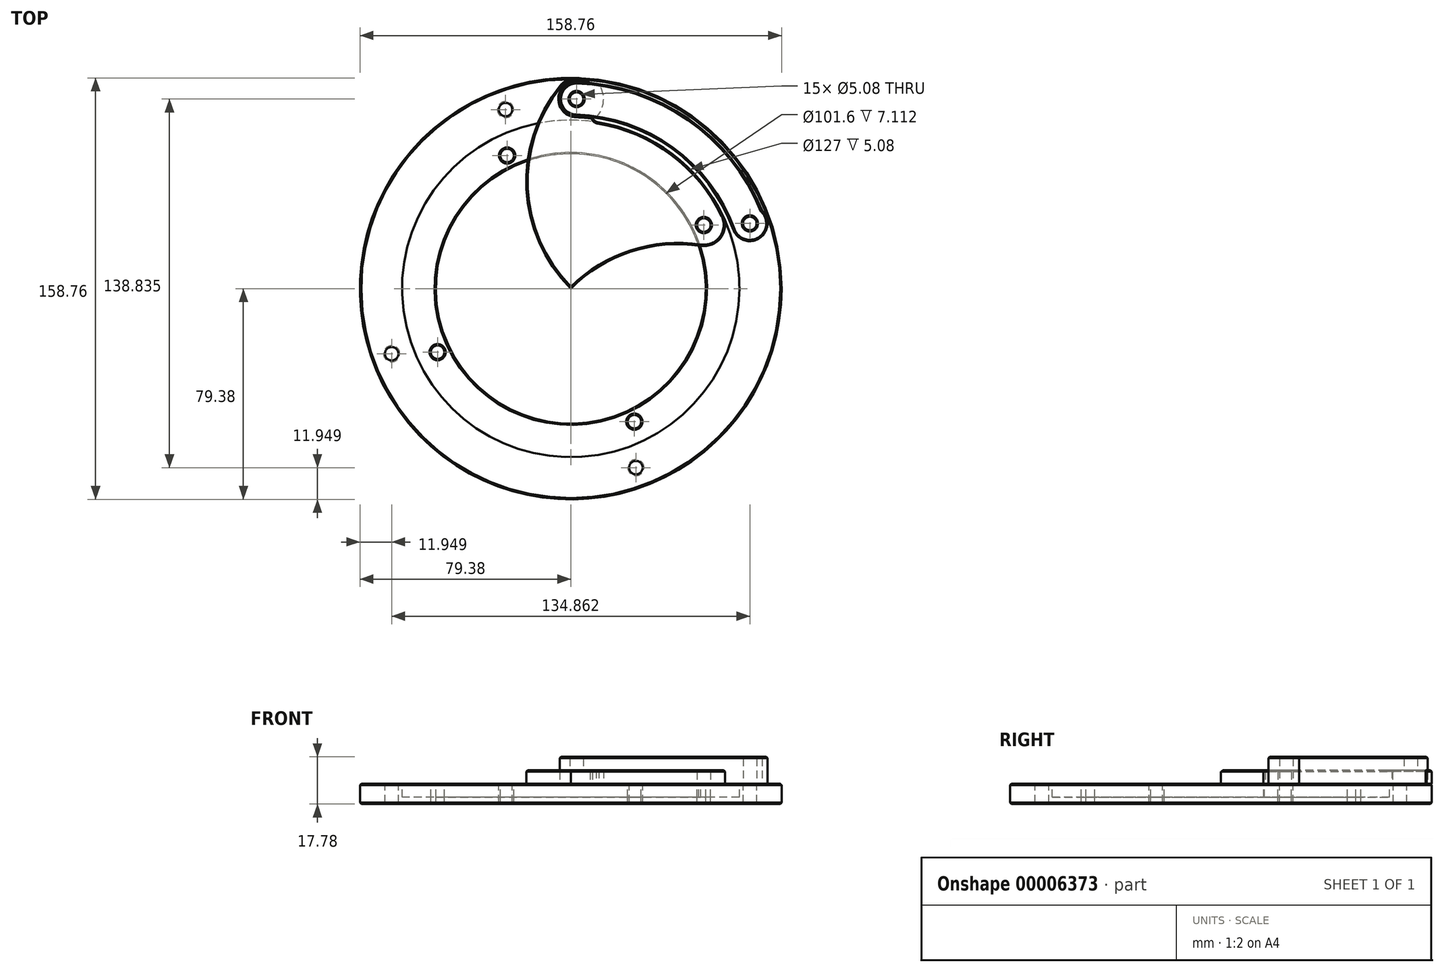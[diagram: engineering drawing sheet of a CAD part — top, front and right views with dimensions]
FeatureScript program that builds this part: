
annotation { "Feature Type Name" : "Feature", "Feature Type Description" : "" }
export const myFeature = defineFeature(function(context is Context, id is Id, definition is map)
    precondition{}
    {
        {
            var Q0;
            Q0=qCreatedBy(makeId("Top.planeOp"),FACE);
            var sketch = newSketch(context, id + "F0", { "sketchPlane" : qUnion([Q0])});
            skCircle(sketch, "E0", {"center": v(0, 0) * mm, "radius": 79.38 * mm});
            skCircle(sketch, "E1", {"center": v(0, 0) * mm, "radius": 63.5 * mm});
            skCircle(sketch, "E2", {"center": v(0, 0) * mm, "radius": 50.8 * mm});
            skLineSegment(sketch, "E3", {"start": v(0, 0) * mm, "end": v(-56.13, 56.13) * mm, "construction": true});
            skLineSegment(sketch, "E4", {"start": v(0, 0) * mm, "end": v(56.13, 56.13) * mm, "construction": true});
            skLineSegment(sketch, "E5", {"start": v(0, 0) * mm, "end": v(56.13, -56.13) * mm, "construction": true});
            skLineSegment(sketch, "E6", {"start": v(0, 0) * mm, "end": v(-56.13, -56.13) * mm, "construction": true});
            skCircle(sketch, "E7", {"center": v(40.41, 40.41) * mm, "radius": 57.15 * mm});
            skCircle(sketch, "E8", {"center": v(40.41, -40.41) * mm, "radius": 57.15 * mm});
            skCircle(sketch, "E9", {"center": v(2.18, 71.4) * mm, "radius": 7.94 * mm});
            skCircle(sketch, "E10", {"center": v(50.14, 23.95) * mm, "radius": 7.94 * mm});
            skCircle(sketch, "E11", {"center": v(2.18, 71.4) * mm, "radius": 2.54 * mm});
            skCircle(sketch, "E12", {"center": v(50.14, 23.95) * mm, "radius": 2.54 * mm});
            skCircle(sketch, "E13", {"center": v(10.61, 65.18) * mm, "radius": 2.54 * mm});
            skSolve(sketch);
        }
        {
            var Q0;
            {var subQ1=sQuery(id+"F0.wireOp",EDGE,"E7");var subQ3=sQuery(id+"F0.wireOp",EDGE,"E2");var subQ5=makeQuery(id+"F0.imprint","INTERSECT",VERTEX,{"disambiguationData":[OD(0.0)],"derivedFrom":[subQ3,subQ1]});Q0=makeQuery(id+"F0.imprint","IMPRINT",FACE,{"disambiguationData":[TD([[makeQuery(id+"F0.imprint","IMPRINT",EDGE,{"disambiguationData":[TD([[subQ5,1.0]])],"derivedFrom":subQ3}),1.0]])]});}
            var Q1;
            {var subQ3=sQuery(id+"F0.wireOp",EDGE,"E1");var subQ8=makeQuery(id+"F0.imprint","INTERSECT",VERTEX,{"derivedFrom":[subQ3,sQuery(id+"F0.wireOp",EDGE,"E9")]});Q1=makeQuery(id+"F0.imprint","IMPRINT",FACE,{"disambiguationData":[TD([[makeQuery(id+"F0.imprint","IMPRINT",EDGE,{"disambiguationData":[TD([[subQ8,1.0]])],"derivedFrom":subQ3}),1.0]])]});}
            var Q2;
            {var subQ0=sQuery(id+"F0.wireOp",EDGE,"E9");var subQ2=makeQuery(id+"F0.imprint","INTERSECT",VERTEX,{"derivedFrom":[sQuery(id+"F0.wireOp",EDGE,"E1"),subQ0]});Q2=makeQuery(id+"F0.imprint","IMPRINT",FACE,{"disambiguationData":[TD([[makeQuery(id+"F0.imprint","IMPRINT",EDGE,{"disambiguationData":[TD([[subQ2,1.0]])],"derivedFrom":subQ0}),1.0]])]});}
            var Q3;
            {var subQ0=sQuery(id+"F0.wireOp",EDGE,"E9");var subQ3=sQuery(id+"F0.wireOp",EDGE,"E1");var subQ4=makeQuery(id+"F0.imprint","INTERSECT",VERTEX,{"derivedFrom":[subQ3,subQ0]});Q3=makeQuery(id+"F0.imprint","IMPRINT",FACE,{"disambiguationData":[TD([[makeQuery(id+"F0.imprint","IMPRINT",EDGE,{"disambiguationData":[TD([[subQ4,-1.0]])],"derivedFrom":subQ3}),-1.0]])]});}
            var Q4;
            {var subQ0=sQuery(id+"F0.wireOp",EDGE,"E13");var subQ3=sQuery(id+"F0.wireOp",EDGE,"E1");var subQ4=makeQuery(id+"F0.imprint","INTERSECT",VERTEX,{"derivedFrom":[subQ3,subQ0]});Q4=makeQuery(id+"F0.imprint","IMPRINT",FACE,{"disambiguationData":[TD([[makeQuery(id+"F0.imprint","IMPRINT",EDGE,{"disambiguationData":[TD([[subQ4,-1.0]])],"derivedFrom":subQ3}),-1.0]])]});}
            var Q5;
            Q5=makeQuery(id+"F0.imprint","IMPRINT",FACE,{"disambiguationData":[TD([[makeQuery(id+"F0.imprint","IMPRINT",EDGE,{"derivedFrom":sQuery(id+"F0.wireOp",EDGE,"E12")}),-1.0]])]});
            var Q6;
            {var subQ0=sQuery(id+"F0.wireOp",EDGE,"E10");var subQ3=sQuery(id+"F0.wireOp",EDGE,"E2");var subQ4=makeQuery(id+"F0.imprint","INTERSECT",VERTEX,{"derivedFrom":[subQ3,subQ0]});Q6=makeQuery(id+"F0.imprint","IMPRINT",FACE,{"disambiguationData":[TD([[makeQuery(id+"F0.imprint","IMPRINT",EDGE,{"disambiguationData":[TD([[subQ4,1.0]])],"derivedFrom":subQ3}),-1.0]])]});}
            var Q7;
            {var subQ0=sQuery(id+"F0.wireOp",EDGE,"E10");var subQ1=sQuery(id+"F0.wireOp",EDGE,"E2");var subQ3=makeQuery(id+"F0.imprint","INTERSECT",VERTEX,{"disambiguationData":[OD(0.0)],"derivedFrom":[subQ1,subQ0]});Q7=makeQuery(id+"F0.imprint","IMPRINT",FACE,{"disambiguationData":[TD([[makeQuery(id+"F0.imprint","IMPRINT",EDGE,{"disambiguationData":[TD([[subQ3,-1.0]])],"derivedFrom":subQ1}),1.0]])]});}
            extrude(context, id + "F1", {"entities" : qUnion([Q0, Q1, Q2, Q3, Q4, Q5, Q6, Q7]), "depth" : 5.08 * mm});
        }
        {
            var Q0;
            {var subQ3=sQuery(id+"F0.wireOp",EDGE,"E0");var subQ5=sQuery(id+"F0.wireOp",EDGE,"E7");var subQ8=makeQuery(id+"F0.imprint","INTERSECT",VERTEX,{"disambiguationData":[OD(0.0)],"derivedFrom":[subQ3,subQ5]});Q0=makeQuery(id+"F0.imprint","IMPRINT",FACE,{"disambiguationData":[TD([[makeQuery(id+"F0.imprint","IMPRINT",EDGE,{"disambiguationData":[TD([[subQ8,-1.0]])],"derivedFrom":subQ3}),1.0]])]});}
            var Q1;
            {var subQ3=sQuery(id+"F0.wireOp",EDGE,"E1");var subQ5=sQuery(id+"F0.wireOp",EDGE,"E7");var subQ7=makeQuery(id+"F0.imprint","INTERSECT",VERTEX,{"disambiguationData":[OD(0.0)],"derivedFrom":[subQ3,subQ5]});Q1=makeQuery(id+"F0.imprint","IMPRINT",FACE,{"disambiguationData":[TD([[makeQuery(id+"F0.imprint","IMPRINT",EDGE,{"disambiguationData":[TD([[subQ7,-1.0]])],"derivedFrom":subQ3}),1.0]])]});}
            var Q2;
            {var subQ0=sQuery(id+"F0.wireOp",EDGE,"E8");var subQ3=sQuery(id+"F0.wireOp",EDGE,"E0");var subQ4=makeQuery(id+"F0.imprint","INTERSECT",VERTEX,{"disambiguationData":[OD(0.0)],"derivedFrom":[subQ3,subQ0]});Q2=makeQuery(id+"F0.imprint","IMPRINT",FACE,{"disambiguationData":[TD([[makeQuery(id+"F0.imprint","IMPRINT",EDGE,{"disambiguationData":[TD([[subQ4,-1.0]])],"derivedFrom":subQ3}),1.0]])]});}
            var Q3;
            {var subQ0=sQuery(id+"F0.wireOp",EDGE,"E8");var subQ3=sQuery(id+"F0.wireOp",EDGE,"E1");var subQ4=makeQuery(id+"F0.imprint","INTERSECT",VERTEX,{"disambiguationData":[OD(1.0)],"derivedFrom":[subQ3,subQ0]});Q3=makeQuery(id+"F0.imprint","IMPRINT",FACE,{"disambiguationData":[TD([[makeQuery(id+"F0.imprint","IMPRINT",EDGE,{"disambiguationData":[TD([[subQ4,-1.0]])],"derivedFrom":subQ3}),1.0]])]});}
            var Q4;
            {var subQ0=sQuery(id+"F0.wireOp",EDGE,"E8");var subQ4=sQuery(id+"F0.wireOp",EDGE,"E1");var subQ5=makeQuery(id+"F0.imprint","INTERSECT",VERTEX,{"disambiguationData":[OD(0.0)],"derivedFrom":[subQ4,subQ0]});Q4=makeQuery(id+"F0.imprint","IMPRINT",FACE,{"disambiguationData":[TD([[makeQuery(id+"F0.imprint","IMPRINT",EDGE,{"disambiguationData":[TD([[subQ5,1.0]])],"derivedFrom":subQ4}),1.0]])]});}
            var Q5;
            {var subQ5=sQuery(id+"F0.wireOp",EDGE,"E7");var subQ9=sQuery(id+"F0.wireOp",EDGE,"E0");var subQ11=makeQuery(id+"F0.imprint","INTERSECT",VERTEX,{"disambiguationData":[OD(0.0)],"derivedFrom":[subQ9,subQ5]});Q5=makeQuery(id+"F0.imprint","IMPRINT",FACE,{"disambiguationData":[TD([[makeQuery(id+"F0.imprint","IMPRINT",EDGE,{"disambiguationData":[TD([[subQ11,1.0]])],"derivedFrom":subQ9}),1.0]])]});}
            var Q6;
            {var subQ0=sQuery(id+"F0.wireOp",EDGE,"E8");var subQ3=sQuery(id+"F0.wireOp",EDGE,"E0");var subQ4=makeQuery(id+"F0.imprint","INTERSECT",VERTEX,{"disambiguationData":[OD(1.0)],"derivedFrom":[subQ3,subQ0]});Q6=makeQuery(id+"F0.imprint","IMPRINT",FACE,{"disambiguationData":[TD([[makeQuery(id+"F0.imprint","IMPRINT",EDGE,{"disambiguationData":[TD([[subQ4,1.0]])],"derivedFrom":subQ3}),1.0]])]});}
            var Q7;
            {var subQ0=sQuery(id+"F0.wireOp",EDGE,"E10");var subQ3=sQuery(id+"F0.wireOp",EDGE,"E1");var subQ4=makeQuery(id+"F0.imprint","INTERSECT",VERTEX,{"derivedFrom":[subQ3,subQ0]});Q7=makeQuery(id+"F0.imprint","IMPRINT",FACE,{"disambiguationData":[TD([[makeQuery(id+"F0.imprint","IMPRINT",EDGE,{"disambiguationData":[TD([[subQ4,1.0]])],"derivedFrom":subQ3}),1.0]])]});}
            var Q8;
            {var subQ0=sQuery(id+"F0.wireOp",EDGE,"E10");var subQ3=sQuery(id+"F0.wireOp",EDGE,"E1");var subQ4=makeQuery(id+"F0.imprint","INTERSECT",VERTEX,{"derivedFrom":[subQ3,subQ0]});Q8=makeQuery(id+"F0.imprint","IMPRINT",FACE,{"disambiguationData":[TD([[makeQuery(id+"F0.imprint","IMPRINT",EDGE,{"disambiguationData":[TD([[subQ4,-1.0]])],"derivedFrom":subQ3}),1.0]])]});}
            var Q9;
            Q9=makeQuery(id+"F0.imprint","IMPRINT",FACE,{"disambiguationData":[TD([[makeQuery(id+"F0.imprint","IMPRINT",EDGE,{"derivedFrom":sQuery(id+"F0.wireOp",EDGE,"E12")}),-1.0]])]});
            var Q10;
            {var subQ0=sQuery(id+"F0.wireOp",EDGE,"E10");var subQ3=sQuery(id+"F0.wireOp",EDGE,"E2");var subQ4=makeQuery(id+"F0.imprint","INTERSECT",VERTEX,{"derivedFrom":[subQ3,subQ0]});Q10=makeQuery(id+"F0.imprint","IMPRINT",FACE,{"disambiguationData":[TD([[makeQuery(id+"F0.imprint","IMPRINT",EDGE,{"disambiguationData":[TD([[subQ4,1.0]])],"derivedFrom":subQ3}),-1.0]])]});}
            var Q11;
            {var subQ0=sQuery(id+"F0.wireOp",EDGE,"E13");var subQ2=makeQuery(id+"F0.imprint","INTERSECT",VERTEX,{"derivedFrom":[sQuery(id+"F0.wireOp",EDGE,"E1"),subQ0]});Q11=makeQuery(id+"F0.imprint","IMPRINT",FACE,{"disambiguationData":[TD([[makeQuery(id+"F0.imprint","IMPRINT",EDGE,{"disambiguationData":[TD([[subQ2,1.0]])],"derivedFrom":subQ0}),1.0]])]});}
            var Q12;
            Q12=makeQuery(id+"F0.imprint","IMPRINT",FACE,{"disambiguationData":[TD([[makeQuery(id+"F0.imprint","IMPRINT",EDGE,{"derivedFrom":sQuery(id+"F0.wireOp",EDGE,"E11")}),-1.0]])]});
            var Q13;
            {var subQ0=sQuery(id+"F0.wireOp",EDGE,"E9");var subQ3=sQuery(id+"F0.wireOp",EDGE,"E1");var subQ4=makeQuery(id+"F0.imprint","INTERSECT",VERTEX,{"derivedFrom":[subQ3,subQ0]});Q13=makeQuery(id+"F0.imprint","IMPRINT",FACE,{"disambiguationData":[TD([[makeQuery(id+"F0.imprint","IMPRINT",EDGE,{"disambiguationData":[TD([[subQ4,-1.0]])],"derivedFrom":subQ3}),-1.0]])]});}
            var Q14;
            {var subQ0=sQuery(id+"F0.wireOp",EDGE,"E13");var subQ3=sQuery(id+"F0.wireOp",EDGE,"E1");var subQ4=makeQuery(id+"F0.imprint","INTERSECT",VERTEX,{"derivedFrom":[subQ3,subQ0]});Q14=makeQuery(id+"F0.imprint","IMPRINT",FACE,{"disambiguationData":[TD([[makeQuery(id+"F0.imprint","IMPRINT",EDGE,{"disambiguationData":[TD([[subQ4,-1.0]])],"derivedFrom":subQ3}),-1.0]])]});}
            var Q15;
            Q15=makeQuery(id+"F0.imprint","IMPRINT",FACE,{"disambiguationData":[TD([[makeQuery(id+"F0.imprint","IMPRINT",EDGE,{"derivedFrom":sQuery(id+"F0.wireOp",EDGE,"E11")}),1.0]])]});
            var Q16;
            {var subQ3=sQuery(id+"F0.wireOp",EDGE,"E0");var subQ6=sQuery(id+"F0.wireOp",EDGE,"E9");var subQ10=makeQuery(id+"F0.imprint","INTERSECT",VERTEX,{"derivedFrom":[subQ3,subQ6]});Q16=makeQuery(id+"F0.imprint","IMPRINT",FACE,{"disambiguationData":[TD([[makeQuery(id+"F0.imprint","IMPRINT",EDGE,{"disambiguationData":[TD([[subQ10,1.0]])],"derivedFrom":subQ3}),1.0]])]});}
            extrude(context, id + "F2", {"entities" : qUnion([Q0, Q1, Q2, Q3, Q4, Q5, Q6, Q7, Q8, Q9, Q10, Q11, Q12, Q13, Q14, Q15, Q16]), "oppositeDirection" : true, "depth" : 7.62 * mm});
        }
        {
            var Q0;
            Q0=qCreatedBy(makeId("Top.planeOp"),FACE);
            var sketch = newSketch(context, id + "F3", { "sketchPlane" : qUnion([Q0])});
            skLineSegment(sketch, "E14", {"start": v(0, 0) * mm, "end": v(126.68, 0) * mm, "construction": true});
            skLineSegment(sketch, "E15", {"start": v(0, 0) * mm, "end": v(115.08, 41.89) * mm, "construction": true});
            skCircle(sketch, "E16", {"center": v(0, 0) * mm, "radius": 71.76 * mm});
            skCircle(sketch, "E17", {"center": v(67.43, 24.54) * mm, "radius": 2.54 * mm});
            skCircle(sketch, "E18", {"center": v(2.18, 71.4) * mm, "radius": 2.54 * mm});
            skCircle(sketch, "E19", {"center": v(2.18, 71.4) * mm, "radius": 6.35 * mm});
            skCircle(sketch, "E20", {"center": v(0, 0) * mm, "radius": 65.09 * mm});
            skCircle(sketch, "E21", {"center": v(0, 0) * mm, "radius": 77.79 * mm});
            skCircle(sketch, "E22", {"center": v(2.18, 71.4) * mm, "radius": 10.16 * mm});
            skCircle(sketch, "E23", {"center": v(67.43, 24.54) * mm, "radius": 6.67 * mm});
            skSolve(sketch);
        }
        {
            var Q0;
            {var subQ0=sQuery(id+"F3.wireOp",EDGE,"E23");var subQ3=sQuery(id+"F3.wireOp",EDGE,"E16");var subQ4=makeQuery(id+"F3.imprint","INTERSECT",VERTEX,{"disambiguationData":[OD(1.0)],"derivedFrom":[subQ3,subQ0]});Q0=makeQuery(id+"F3.imprint","IMPRINT",FACE,{"disambiguationData":[TD([[makeQuery(id+"F3.imprint","IMPRINT",EDGE,{"disambiguationData":[TD([[subQ4,-1.0]])],"derivedFrom":subQ3}),1.0]])]});}
            var Q1;
            {var subQ2=sQuery(id+"F3.wireOp",EDGE,"E16");var subQ5=sQuery(id+"F3.wireOp",EDGE,"E17");var subQ7=makeQuery(id+"F3.imprint","INTERSECT",VERTEX,{"disambiguationData":[OD(0.0)],"derivedFrom":[subQ2,subQ5]});Q1=makeQuery(id+"F3.imprint","IMPRINT",FACE,{"disambiguationData":[TD([[makeQuery(id+"F3.imprint","IMPRINT",EDGE,{"disambiguationData":[TD([[subQ7,1.0]])],"derivedFrom":subQ2}),1.0]])]});}
            var Q2;
            {var subQ1=sQuery(id+"F3.wireOp",EDGE,"E16");var subQ7=sQuery(id+"F3.wireOp",EDGE,"E17");var subQ9=makeQuery(id+"F3.imprint","INTERSECT",VERTEX,{"disambiguationData":[OD(0.0)],"derivedFrom":[subQ1,subQ7]});Q2=makeQuery(id+"F3.imprint","IMPRINT",FACE,{"disambiguationData":[TD([[makeQuery(id+"F3.imprint","IMPRINT",EDGE,{"disambiguationData":[TD([[subQ9,1.0]])],"derivedFrom":subQ1}),-1.0]])]});}
            var Q3;
            {var subQ0=sQuery(id+"F3.wireOp",EDGE,"E23");var subQ1=sQuery(id+"F3.wireOp",EDGE,"E16");var subQ2=makeQuery(id+"F3.imprint","INTERSECT",VERTEX,{"disambiguationData":[OD(1.0)],"derivedFrom":[subQ1,subQ0]});Q3=makeQuery(id+"F3.imprint","IMPRINT",FACE,{"disambiguationData":[TD([[makeQuery(id+"F3.imprint","IMPRINT",EDGE,{"disambiguationData":[TD([[subQ2,-1.0]])],"derivedFrom":subQ1}),-1.0]])]});}
            var Q4;
            {var subQ0=sQuery(id+"F3.wireOp",EDGE,"E23");var subQ1=sQuery(id+"F3.wireOp",EDGE,"E21");var subQ3=makeQuery(id+"F3.imprint","INTERSECT",VERTEX,{"disambiguationData":[OD(0.0)],"derivedFrom":[subQ1,subQ0]});Q4=makeQuery(id+"F3.imprint","IMPRINT",FACE,{"disambiguationData":[TD([[makeQuery(id+"F3.imprint","IMPRINT",EDGE,{"disambiguationData":[TD([[subQ3,1.0]])],"derivedFrom":subQ1}),-1.0]])]});}
            var Q5;
            {var subQ0=sQuery(id+"F3.wireOp",EDGE,"E22");var subQ1=sQuery(id+"F3.wireOp",EDGE,"E16");var subQ2=makeQuery(id+"F3.imprint","INTERSECT",VERTEX,{"disambiguationData":[OD(0.0)],"derivedFrom":[subQ1,subQ0]});Q5=makeQuery(id+"F3.imprint","IMPRINT",FACE,{"disambiguationData":[TD([[makeQuery(id+"F3.imprint","IMPRINT",EDGE,{"disambiguationData":[TD([[subQ2,-1.0]])],"derivedFrom":subQ1}),-1.0]])]});}
            var Q6;
            {var subQ0=sQuery(id+"F3.wireOp",EDGE,"E19");var subQ2=sQuery(id+"F3.wireOp",EDGE,"E16");var subQ3=makeQuery(id+"F3.imprint","INTERSECT",VERTEX,{"disambiguationData":[OD(0.0)],"derivedFrom":[subQ2,subQ0]});Q6=makeQuery(id+"F3.imprint","IMPRINT",FACE,{"disambiguationData":[TD([[makeQuery(id+"F3.imprint","IMPRINT",EDGE,{"disambiguationData":[TD([[subQ3,-1.0]])],"derivedFrom":subQ2}),-1.0]])]});}
            var Q7;
            {var subQ0=sQuery(id+"F3.wireOp",EDGE,"E19");var subQ2=sQuery(id+"F3.wireOp",EDGE,"E16");var subQ3=makeQuery(id+"F3.imprint","INTERSECT",VERTEX,{"disambiguationData":[OD(0.0)],"derivedFrom":[subQ2,subQ0]});Q7=makeQuery(id+"F3.imprint","IMPRINT",FACE,{"disambiguationData":[TD([[makeQuery(id+"F3.imprint","IMPRINT",EDGE,{"disambiguationData":[TD([[subQ3,-1.0]])],"derivedFrom":subQ2}),1.0]])]});}
            var Q8;
            {var subQ0=sQuery(id+"F3.wireOp",EDGE,"E22");var subQ3=sQuery(id+"F3.wireOp",EDGE,"E16");var subQ4=makeQuery(id+"F3.imprint","INTERSECT",VERTEX,{"disambiguationData":[OD(0.0)],"derivedFrom":[subQ3,subQ0]});Q8=makeQuery(id+"F3.imprint","IMPRINT",FACE,{"disambiguationData":[TD([[makeQuery(id+"F3.imprint","IMPRINT",EDGE,{"disambiguationData":[TD([[subQ4,-1.0]])],"derivedFrom":subQ3}),1.0]])]});}
            extrude(context, id + "F4", {"entities" : qUnion([Q0, Q1, Q2, Q3, Q4, Q5, Q6, Q7, Q8]), "depth" : 10.16 * mm});
        }
        {
            var Q0;
            {var subQ0=sQuery(id+"F3.wireOp",EDGE,"E19");var subQ2=sQuery(id+"F3.wireOp",EDGE,"E16");var subQ3=makeQuery(id+"F3.imprint","INTERSECT",VERTEX,{"disambiguationData":[OD(0.0)],"derivedFrom":[subQ2,subQ0]});Q0=makeQuery(id+"F3.imprint","IMPRINT",FACE,{"disambiguationData":[TD([[makeQuery(id+"F3.imprint","IMPRINT",EDGE,{"disambiguationData":[TD([[subQ3,-1.0]])],"derivedFrom":subQ2}),1.0]])]});}
            var Q1;
            {var subQ0=sQuery(id+"F3.wireOp",EDGE,"E19");var subQ2=sQuery(id+"F3.wireOp",EDGE,"E16");var subQ3=makeQuery(id+"F3.imprint","INTERSECT",VERTEX,{"disambiguationData":[OD(0.0)],"derivedFrom":[subQ2,subQ0]});Q1=makeQuery(id+"F3.imprint","IMPRINT",FACE,{"disambiguationData":[TD([[makeQuery(id+"F3.imprint","IMPRINT",EDGE,{"disambiguationData":[TD([[subQ3,-1.0]])],"derivedFrom":subQ2}),-1.0]])]});}
            var Q2;
            {var subQ0=sQuery(id+"F3.wireOp",EDGE,"E22");var subQ1=sQuery(id+"F3.wireOp",EDGE,"E16");var subQ2=makeQuery(id+"F3.imprint","INTERSECT",VERTEX,{"disambiguationData":[OD(0.0)],"derivedFrom":[subQ1,subQ0]});Q2=makeQuery(id+"F3.imprint","IMPRINT",FACE,{"disambiguationData":[TD([[makeQuery(id+"F3.imprint","IMPRINT",EDGE,{"disambiguationData":[TD([[subQ2,-1.0]])],"derivedFrom":subQ1}),-1.0]])]});}
            var Q3;
            {var subQ0=sQuery(id+"F3.wireOp",EDGE,"E22");var subQ3=sQuery(id+"F3.wireOp",EDGE,"E16");var subQ4=makeQuery(id+"F3.imprint","INTERSECT",VERTEX,{"disambiguationData":[OD(0.0)],"derivedFrom":[subQ3,subQ0]});Q3=makeQuery(id+"F3.imprint","IMPRINT",FACE,{"disambiguationData":[TD([[makeQuery(id+"F3.imprint","IMPRINT",EDGE,{"disambiguationData":[TD([[subQ4,-1.0]])],"derivedFrom":subQ3}),1.0]])]});}
            extrude(context, id + "F5", {"entities" : qUnion([Q0, Q1, Q2, Q3]), "operationType" : NewBodyOperationType.REMOVE, "depth" : 5.08 * mm});
        }
        {
            var Q0;
            {var subQ0=sQuery(id+"F3.wireOp",EDGE,"E17");var subQ1=sQuery(id+"F3.wireOp",EDGE,"E16");var subQ3=makeQuery(id+"F3.imprint","INTERSECT",VERTEX,{"disambiguationData":[OD(0.0)],"derivedFrom":[subQ1,subQ0]});Q0=makeQuery(id+"F3.imprint","IMPRINT",FACE,{"disambiguationData":[TD([[makeQuery(id+"F3.imprint","IMPRINT",EDGE,{"disambiguationData":[TD([[subQ3,-1.0]])],"derivedFrom":subQ1}),-1.0]])]});}
            var Q1;
            {var subQ0=sQuery(id+"F3.wireOp",EDGE,"E17");var subQ1=sQuery(id+"F3.wireOp",EDGE,"E16");var subQ3=makeQuery(id+"F3.imprint","INTERSECT",VERTEX,{"disambiguationData":[OD(0.0)],"derivedFrom":[subQ1,subQ0]});Q1=makeQuery(id+"F3.imprint","IMPRINT",FACE,{"disambiguationData":[TD([[makeQuery(id+"F3.imprint","IMPRINT",EDGE,{"disambiguationData":[TD([[subQ3,-1.0]])],"derivedFrom":subQ1}),1.0]])]});}
            extrude(context, id + "F6", {"entities" : qUnion([Q0, Q1]), "operationType" : NewBodyOperationType.REMOVE, "oppositeDirection" : true, "depth" : 25.4 * mm});
        }
        {
            var Q0;
            Q0=qCreatedBy(makeId("Front.planeOp"),FACE);
            var sketch = newSketch(context, id + "F7", { "sketchPlane" : qUnion([Q0])});
            skLineSegment(sketch, "E24", {"start": v(0, 0) * mm, "end": v(0, 39.3) * mm, "construction": true});
            skSolve(sketch);
        }
        {
            var Q0;
            {var subQ0=sQuery(id+"F0.wireOp",EDGE,"E10");var subQ3=sQuery(id+"F0.wireOp",EDGE,"E1");var subQ4=makeQuery(id+"F0.imprint","INTERSECT",VERTEX,{"derivedFrom":[subQ3,subQ0]});Q0=makeQuery(id+"F0.imprint","IMPRINT",FACE,{"disambiguationData":[TD([[makeQuery(id+"F0.imprint","IMPRINT",EDGE,{"disambiguationData":[TD([[subQ4,-1.0]])],"derivedFrom":subQ3}),1.0]])]});}
            var Q1;
            Q1=makeQuery(id+"F0.imprint","IMPRINT",FACE,{"disambiguationData":[TD([[makeQuery(id+"F0.imprint","IMPRINT",EDGE,{"derivedFrom":sQuery(id+"F0.wireOp",EDGE,"E12")}),-1.0]])]});
            var Q2;
            {var subQ0=sQuery(id+"F0.wireOp",EDGE,"E8");var subQ4=sQuery(id+"F0.wireOp",EDGE,"E1");var subQ5=makeQuery(id+"F0.imprint","INTERSECT",VERTEX,{"disambiguationData":[OD(0.0)],"derivedFrom":[subQ4,subQ0]});Q2=makeQuery(id+"F0.imprint","IMPRINT",FACE,{"disambiguationData":[TD([[makeQuery(id+"F0.imprint","IMPRINT",EDGE,{"disambiguationData":[TD([[subQ5,1.0]])],"derivedFrom":subQ4}),1.0]])]});}
            var Q3;
            {var subQ0=sQuery(id+"F0.wireOp",EDGE,"E10");var subQ3=sQuery(id+"F0.wireOp",EDGE,"E1");var subQ4=makeQuery(id+"F0.imprint","INTERSECT",VERTEX,{"derivedFrom":[subQ3,subQ0]});Q3=makeQuery(id+"F0.imprint","IMPRINT",FACE,{"disambiguationData":[TD([[makeQuery(id+"F0.imprint","IMPRINT",EDGE,{"disambiguationData":[TD([[subQ4,1.0]])],"derivedFrom":subQ3}),1.0]])]});}
            var Q4;
            {var subQ0=sQuery(id+"F0.wireOp",EDGE,"E8");var subQ3=sQuery(id+"F0.wireOp",EDGE,"E1");var subQ4=makeQuery(id+"F0.imprint","INTERSECT",VERTEX,{"disambiguationData":[OD(1.0)],"derivedFrom":[subQ3,subQ0]});Q4=makeQuery(id+"F0.imprint","IMPRINT",FACE,{"disambiguationData":[TD([[makeQuery(id+"F0.imprint","IMPRINT",EDGE,{"disambiguationData":[TD([[subQ4,-1.0]])],"derivedFrom":subQ3}),1.0]])]});}
            var Q5;
            {var subQ3=sQuery(id+"F0.wireOp",EDGE,"E1");var subQ5=sQuery(id+"F0.wireOp",EDGE,"E7");var subQ7=makeQuery(id+"F0.imprint","INTERSECT",VERTEX,{"disambiguationData":[OD(0.0)],"derivedFrom":[subQ3,subQ5]});Q5=makeQuery(id+"F0.imprint","IMPRINT",FACE,{"disambiguationData":[TD([[makeQuery(id+"F0.imprint","IMPRINT",EDGE,{"disambiguationData":[TD([[subQ7,-1.0]])],"derivedFrom":subQ3}),1.0]])]});}
            extrude(context, id + "F8", {"entities" : qUnion([Q0, Q1, Q2, Q3, Q4, Q5]), "oppositeDirection" : true, "depth" : 5.08 * mm});
        }
        {
            var Q0;
            Q0=makeQuery(id+"F2.opExtrude","SWEPT_FACE",FACE,{"disambiguationData":[OSD([sQuery(id+"F0.wireOp",EDGE,"E12")])]});
            var Q1;
            Q1=makeQuery(id+"F6.boolean.opBoolean","COPY",FACE,{"derivedFrom":makeQuery(id+"F6.opExtrude","SWEPT_FACE",FACE,{"disambiguationData":[OSD([sQuery(id+"F3.wireOp",EDGE,"E17")])]})});
            var Q2;
            Q2=makeQuery(id+"F2.opExtrude","SWEPT_BODY",BODY,{"disambiguationData":[OSD([sQuery(id+"F0.wireOp",EDGE,"E0"),sQuery(id+"F0.wireOp",EDGE,"E2"),sQuery(id+"F0.wireOp",EDGE,"E12")])]});
            var Q3;
            Q3=sQuery(id+"F7.wireOp",EDGE,"E24");
            circularPattern(context, id + "F9", {"faces" : qUnion([Q0, Q1]), "axis" : qUnion([Q3]), "angle" : 90 * degree, "instanceCount" : 4, "patternType" : PatternType.FACE});
        }
        {
            var Q0;
            Q0=makeQuery(id+"F8.opExtrude","SWEPT_BODY",BODY,{"disambiguationData":[OSD([sQuery(id+"F0.wireOp",EDGE,"E1"),sQuery(id+"F0.wireOp",EDGE,"E2"),sQuery(id+"F0.wireOp",EDGE,"E8"),sQuery(id+"F0.wireOp",EDGE,"E10"),sQuery(id+"F0.wireOp",EDGE,"E12")])]});
            var Q1;
            Q1=makeQuery(id+"F1.opExtrude","SWEPT_BODY",BODY,{"disambiguationData":[OSD([sQuery(id+"F0.wireOp",EDGE,"E1"),sQuery(id+"F0.wireOp",EDGE,"E7"),sQuery(id+"F0.wireOp",EDGE,"E8"),sQuery(id+"F0.wireOp",EDGE,"E9"),sQuery(id+"F0.wireOp",EDGE,"E10"),sQuery(id+"F0.wireOp",EDGE,"E11"),sQuery(id+"F0.wireOp",EDGE,"E12"),sQuery(id+"F0.wireOp",EDGE,"E13")])]});
            booleanBodies(context, id + "F10", {"operationType" : BooleanOperationType.SUBTRACTION, "tools" : qUnion([Q0]), "targets" : qUnion([Q1]), "keepTools" : true});
        }
        {
            var Q0;
            Q0=makeQuery(id+"F8.opExtrude","SWEPT_BODY",BODY,{"disambiguationData":[OSD([sQuery(id+"F0.wireOp",EDGE,"E1"),sQuery(id+"F0.wireOp",EDGE,"E2"),sQuery(id+"F0.wireOp",EDGE,"E8"),sQuery(id+"F0.wireOp",EDGE,"E10"),sQuery(id+"F0.wireOp",EDGE,"E12")])]});
            var Q1;
            Q1=makeQuery(id+"F2.opExtrude","SWEPT_BODY",BODY,{"disambiguationData":[OSD([sQuery(id+"F0.wireOp",EDGE,"E0"),sQuery(id+"F0.wireOp",EDGE,"E2"),sQuery(id+"F0.wireOp",EDGE,"E12")])]});
            booleanBodies(context, id + "F11", {"operationType" : BooleanOperationType.SUBTRACTION, "tools" : qUnion([Q0]), "targets" : qUnion([Q1]), "keepTools" : true});
        }
        {
            var Q0;
            Q0=makeQuery(id+"F8.opExtrude","SWEPT_FACE",FACE,{"disambiguationData":[OSD([sQuery(id+"F0.wireOp",EDGE,"E12")])]});
            var Q1;
            Q1=sQuery(id+"F7.wireOp",EDGE,"E24");
            circularPattern(context, id + "F12", {"faces" : qUnion([Q0]), "axis" : qUnion([Q1]), "angle" : 90 * degree, "instanceCount" : 4, "patternType" : PatternType.FACE});
        }
        {
            var Q0;
            Q0=makeQuery(id+"F2.opExtrude","CAP_EDGE",EDGE,{"disambiguationData":[OSD([sQuery(id+"F0.wireOp",EDGE,"E0")])],"isStart":true});
            var Q1;
            Q1=makeQuery(id+"F9.opPattern","COPY",EDGE,{"derivedFrom":makeQuery(id+"F6.boolean.opBoolean","COPY",EDGE,{"derivedFrom":makeQuery(id+"F6.opExtrude","CAP_EDGE",EDGE,{"disambiguationData":[OSD([sQuery(id+"F3.wireOp",EDGE,"E17")])],"isStart":true})}),"instanceName":"2"});
            var Q2;
            Q2=makeQuery(id+"F12.opPattern","COPY",EDGE,{"derivedFrom":makeQuery(id+"F8.opExtrude","CAP_EDGE",EDGE,{"disambiguationData":[OSD([sQuery(id+"F0.wireOp",EDGE,"E12")])],"isStart":true}),"instanceName":"2"});
            var Q3;
            Q3=makeQuery(id+"F9.opPattern","COPY",EDGE,{"derivedFrom":makeQuery(id+"F6.boolean.opBoolean","COPY",EDGE,{"derivedFrom":makeQuery(id+"F6.opExtrude","CAP_EDGE",EDGE,{"disambiguationData":[OSD([sQuery(id+"F3.wireOp",EDGE,"E17")])],"isStart":true})}),"instanceName":"3"});
            var Q4;
            Q4=makeQuery(id+"F12.opPattern","COPY",EDGE,{"derivedFrom":makeQuery(id+"F8.opExtrude","CAP_EDGE",EDGE,{"disambiguationData":[OSD([sQuery(id+"F0.wireOp",EDGE,"E12")])],"isStart":true}),"instanceName":"3"});
            var Q5;
            Q5=makeQuery(id+"F1.opExtrude","CAP_FACE",FACE,{"disambiguationData":[OSD([sQuery(id+"F0.wireOp",EDGE,"E1"),sQuery(id+"F0.wireOp",EDGE,"E7"),sQuery(id+"F0.wireOp",EDGE,"E8"),sQuery(id+"F0.wireOp",EDGE,"E9"),sQuery(id+"F0.wireOp",EDGE,"E10"),sQuery(id+"F0.wireOp",EDGE,"E11"),sQuery(id+"F0.wireOp",EDGE,"E12"),sQuery(id+"F0.wireOp",EDGE,"E13")])],"isStart":false});
            var Q6;
            Q6=makeQuery(id+"F4.opExtrude","CAP_FACE",FACE,{"disambiguationData":[OSD([sQuery(id+"F3.wireOp",EDGE,"E17"),sQuery(id+"F3.wireOp",EDGE,"E18"),sQuery(id+"F3.wireOp",EDGE,"E19"),sQuery(id+"F3.wireOp",EDGE,"E20"),sQuery(id+"F3.wireOp",EDGE,"E21"),sQuery(id+"F3.wireOp",EDGE,"E23")])],"isStart":false});
            var Q7;
            Q7=makeQuery(id+"F2.opExtrude","CAP_FACE",FACE,{"disambiguationData":[OSD([sQuery(id+"F0.wireOp",EDGE,"E0"),sQuery(id+"F0.wireOp",EDGE,"E2"),sQuery(id+"F0.wireOp",EDGE,"E12")])],"isStart":false});
            var Q8;
            Q8=makeQuery(id+"F12.opPattern","COPY",EDGE,{"derivedFrom":makeQuery(id+"F8.opExtrude","CAP_EDGE",EDGE,{"disambiguationData":[OSD([sQuery(id+"F0.wireOp",EDGE,"E12")])],"isStart":true}),"instanceName":"1"});
            var Q9;
            Q9=makeQuery(id+"F9.opPattern","COPY",EDGE,{"derivedFrom":makeQuery(id+"F6.boolean.opBoolean","COPY",EDGE,{"derivedFrom":makeQuery(id+"F6.opExtrude","CAP_EDGE",EDGE,{"disambiguationData":[OSD([sQuery(id+"F3.wireOp",EDGE,"E17")])],"isStart":true})}),"instanceName":"1"});
            var Q10;
            Q10=makeQuery(id+"F8.opExtrude","CAP_EDGE",EDGE,{"disambiguationData":[OSD([sQuery(id+"F0.wireOp",EDGE,"E2")])],"isStart":true});
            chamfer(context, id + "F13", {"entities" : qUnion([Q0, Q1, Q2, Q3, Q4, Q5, Q6, Q7, Q8, Q9, Q10]), "width" : 0.5 * mm, "tangentPropagation" : true});
        }
    });
